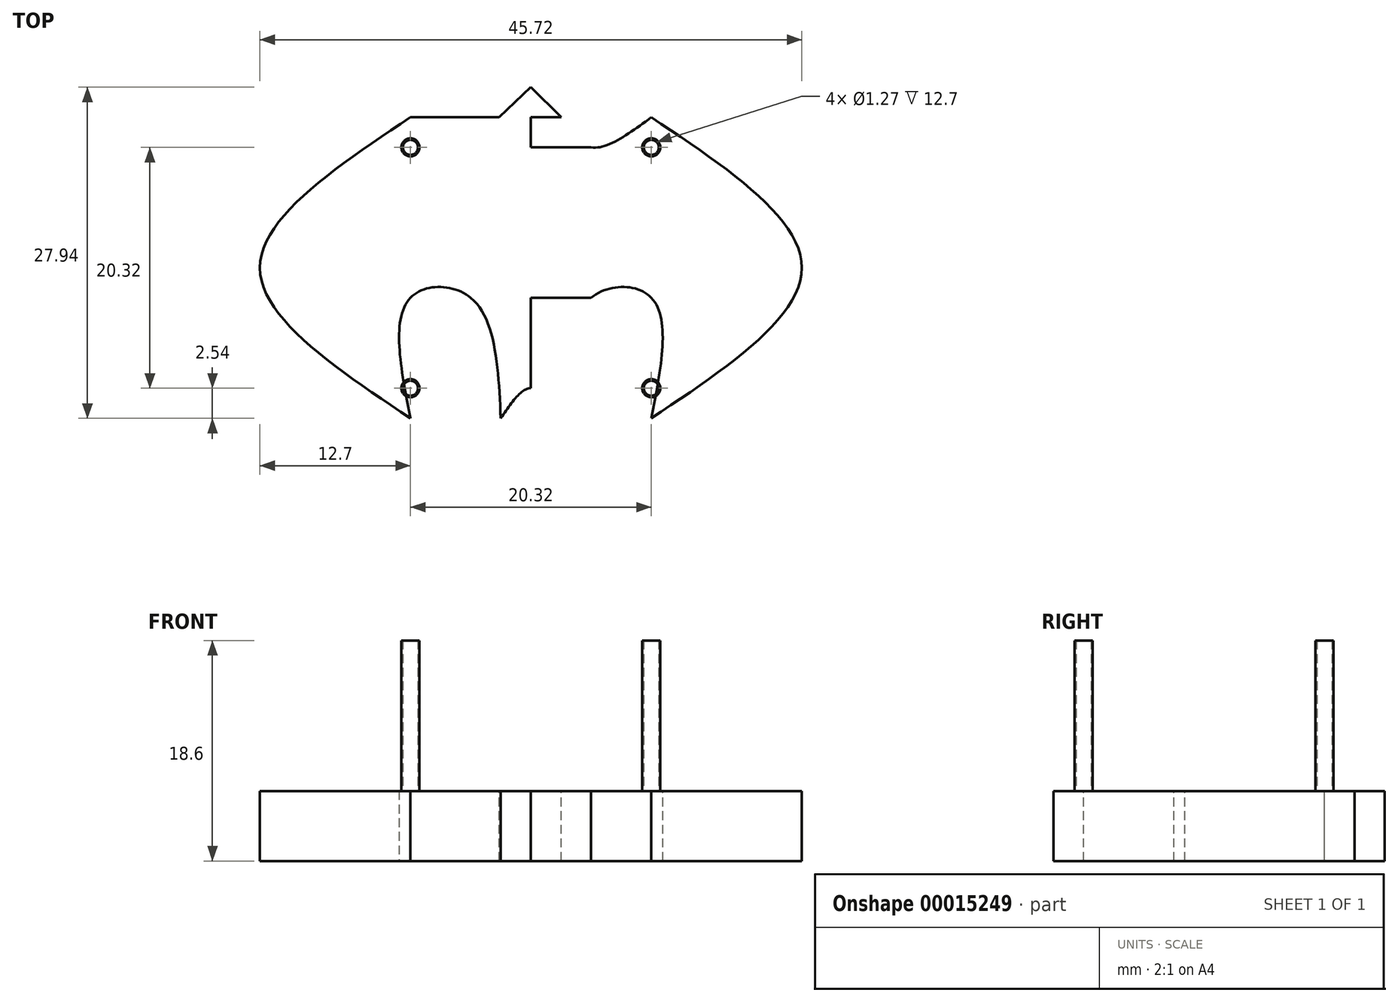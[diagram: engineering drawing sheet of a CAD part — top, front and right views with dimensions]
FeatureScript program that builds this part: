
annotation { "Feature Type Name" : "Feature", "Feature Type Description" : "" }
export const myFeature = defineFeature(function(context is Context, id is Id, definition is map)
    precondition{}
    {
        {
            var Q0;
            Q0=qCreatedBy(makeId("Top.planeOp"),FACE);
            var sketch = newSketch(context, id + "F0", { "sketchPlane" : qUnion([Q0])});
            skLineSegment(sketch, "E0.rect.bottom", {"start": v(10.16, 10.16) * mm, "end": v(-10.16, 10.16) * mm});
            skLineSegment(sketch, "E0.rect.top", {"start": v(10.16, -10.16) * mm, "end": v(-10.16, -10.16) * mm});
            skLineSegment(sketch, "E0.rect.left", {"start": v(10.16, 10.16) * mm, "end": v(10.16, -10.16) * mm});
            skLineSegment(sketch, "E0.rect.right", {"start": v(-10.16, 10.16) * mm, "end": v(-10.16, -10.16) * mm});
            skPoint(sketch, "E0.rect.middle", {"position": v(0, 0) * mm});
            skCircle(sketch, "E1", {"center": v(-10.16, 10.16) * mm, "radius": 0.64 * mm});
            skCircle(sketch, "E2", {"center": v(10.16, 10.16) * mm, "radius": 0.64 * mm});
            skCircle(sketch, "E3", {"center": v(-10.16, -10.16) * mm, "radius": 0.64 * mm});
            skCircle(sketch, "E4", {"center": v(10.16, -10.16) * mm, "radius": 0.64 * mm});
            skLineSegment(sketch, "E5", {"start": v(0, 0) * mm, "end": v(0, -12.7) * mm});
            skLineSegment(sketch, "E6", {"start": v(0, 0) * mm, "end": v(0, 12.7) * mm});
            skCircle(sketch, "E7", {"center": v(-10.16, 10.16) * mm, "radius": 0.76 * mm});
            skCircle(sketch, "E8", {"center": v(10.16, 10.16) * mm, "radius": 0.76 * mm});
            skCircle(sketch, "E9", {"center": v(-10.16, -10.16) * mm, "radius": 0.76 * mm});
            skCircle(sketch, "E10", {"center": v(10.16, -10.16) * mm, "radius": 0.76 * mm});
            skSolve(sketch);
        }
        {
            var Q0;
            {var subQ0=sQuery(id+"F0.wireOp",EDGE,"E9");var subQ3=sQuery(id+"F0.wireOp",EDGE,"E0.rect.top");var subQ4=makeQuery(id+"F0.imprint","INTERSECT",VERTEX,{"derivedFrom":[subQ3,subQ0]});Q0=makeQuery(id+"F0.imprint","IMPRINT",FACE,{"disambiguationData":[TD([[makeQuery(id+"F0.imprint","IMPRINT",EDGE,{"disambiguationData":[TD([[subQ4,-1.0]])],"derivedFrom":subQ3}),1.0]])]});}
            var Q1;
            {var subQ0=sQuery(id+"F0.wireOp",EDGE,"E10");var subQ3=sQuery(id+"F0.wireOp",EDGE,"E0.rect.top");var subQ4=makeQuery(id+"F0.imprint","INTERSECT",VERTEX,{"derivedFrom":[subQ3,subQ0]});Q1=makeQuery(id+"F0.imprint","IMPRINT",FACE,{"disambiguationData":[TD([[makeQuery(id+"F0.imprint","IMPRINT",EDGE,{"disambiguationData":[TD([[subQ4,1.0]])],"derivedFrom":subQ3}),-1.0]])]});}
            var Q2;
            {var subQ0=sQuery(id+"F0.wireOp",EDGE,"E9");var subQ3=sQuery(id+"F0.wireOp",EDGE,"E0.rect.top");var subQ4=makeQuery(id+"F0.imprint","INTERSECT",VERTEX,{"derivedFrom":[subQ3,subQ0]});Q2=makeQuery(id+"F0.imprint","IMPRINT",FACE,{"disambiguationData":[TD([[makeQuery(id+"F0.imprint","IMPRINT",EDGE,{"disambiguationData":[TD([[subQ4,-1.0]])],"derivedFrom":subQ3}),-1.0]])]});}
            var Q3;
            {var subQ0=sQuery(id+"F0.wireOp",EDGE,"E10");var subQ3=sQuery(id+"F0.wireOp",EDGE,"E0.rect.top");var subQ4=makeQuery(id+"F0.imprint","INTERSECT",VERTEX,{"derivedFrom":[subQ3,subQ0]});Q3=makeQuery(id+"F0.imprint","IMPRINT",FACE,{"disambiguationData":[TD([[makeQuery(id+"F0.imprint","IMPRINT",EDGE,{"disambiguationData":[TD([[subQ4,1.0]])],"derivedFrom":subQ3}),1.0]])]});}
            var Q4;
            {var subQ0=sQuery(id+"F0.wireOp",EDGE,"E7");var subQ3=sQuery(id+"F0.wireOp",EDGE,"E0.rect.bottom");var subQ4=makeQuery(id+"F0.imprint","INTERSECT",VERTEX,{"derivedFrom":[subQ3,subQ0]});Q4=makeQuery(id+"F0.imprint","IMPRINT",FACE,{"disambiguationData":[TD([[makeQuery(id+"F0.imprint","IMPRINT",EDGE,{"disambiguationData":[TD([[subQ4,-1.0]])],"derivedFrom":subQ3}),1.0]])]});}
            var Q5;
            {var subQ0=sQuery(id+"F0.wireOp",EDGE,"E7");var subQ3=sQuery(id+"F0.wireOp",EDGE,"E0.rect.bottom");var subQ4=makeQuery(id+"F0.imprint","INTERSECT",VERTEX,{"derivedFrom":[subQ3,subQ0]});Q5=makeQuery(id+"F0.imprint","IMPRINT",FACE,{"disambiguationData":[TD([[makeQuery(id+"F0.imprint","IMPRINT",EDGE,{"disambiguationData":[TD([[subQ4,-1.0]])],"derivedFrom":subQ3}),-1.0]])]});}
            var Q6;
            {var subQ0=sQuery(id+"F0.wireOp",EDGE,"E8");var subQ3=sQuery(id+"F0.wireOp",EDGE,"E0.rect.bottom");var subQ4=makeQuery(id+"F0.imprint","INTERSECT",VERTEX,{"derivedFrom":[subQ3,subQ0]});Q6=makeQuery(id+"F0.imprint","IMPRINT",FACE,{"disambiguationData":[TD([[makeQuery(id+"F0.imprint","IMPRINT",EDGE,{"disambiguationData":[TD([[subQ4,1.0]])],"derivedFrom":subQ3}),-1.0]])]});}
            var Q7;
            {var subQ0=sQuery(id+"F0.wireOp",EDGE,"E8");var subQ3=sQuery(id+"F0.wireOp",EDGE,"E0.rect.bottom");var subQ4=makeQuery(id+"F0.imprint","INTERSECT",VERTEX,{"derivedFrom":[subQ3,subQ0]});Q7=makeQuery(id+"F0.imprint","IMPRINT",FACE,{"disambiguationData":[TD([[makeQuery(id+"F0.imprint","IMPRINT",EDGE,{"disambiguationData":[TD([[subQ4,1.0]])],"derivedFrom":subQ3}),1.0]])]});}
            extrude(context, id + "F1", {"entities" : qUnion([Q0, Q1, Q2, Q3, Q4, Q5, Q6, Q7]), "depth" : 12.7 * mm});
        }
        {
            var Q0;
            Q0=qCreatedBy(makeId("Top.planeOp"),FACE);
            var sketch = newSketch(context, id + "F2", { "sketchPlane" : qUnion([Q0])});
            skLineSegment(sketch, "E11", {"start": v(0, 0) * mm, "end": v(-22.86, 0) * mm});
            skLineSegment(sketch, "E12", {"start": v(0, 0) * mm, "end": v(22.86, 0) * mm});
            skLineSegment(sketch, "E13", {"start": v(0, 0) * mm, "end": v(0, 12.7) * mm});
            skLineSegment(sketch, "E14", {"start": v(0, 0) * mm, "end": v(0, -12.7) * mm});
            skLineSegment(sketch, "E15", {"start": v(0, 12.7) * mm, "end": v(-10.16, 12.7) * mm});
            skLineSegment(sketch, "E16", {"start": v(0, 12.7) * mm, "end": v(10.16, 12.7) * mm});
            skLineSegment(sketch, "E17", {"start": v(0, -12.7) * mm, "end": v(-10.16, -12.7) * mm});
            skLineSegment(sketch, "E18", {"start": v(0, -12.7) * mm, "end": v(10.16, -12.7) * mm});
            skFitSpline(sketch, "E19", {"points": [v(-10.16, 12.7) * mm, v(-22.86, 0) * mm, v(-10.16, -12.7) * mm], "startDerivative": vector(-38.1, -25.4) * mm, "endDerivative": vector(38.1, -25.4) * mm});
            skFitSpline(sketch, "E20", {"points": [v(10.16, -12.7) * mm, v(22.86, 0) * mm, v(10.16, 12.7) * mm], "startDerivative": vector(38.1, 25.4) * mm, "endDerivative": vector(-38.1, 25.4) * mm});
            skLineSegment(sketch, "E21", {"start": v(0, -2.53) * mm, "end": v(-10.16, -2.53) * mm});
            skLineSegment(sketch, "E22", {"start": v(0, 2.54) * mm, "end": v(-10.16, 2.54) * mm});
            skLineSegment(sketch, "E23", {"start": v(0, -2.53) * mm, "end": v(10.16, -2.53) * mm});
            skLineSegment(sketch, "E24", {"start": v(0, -12.7) * mm, "end": v(-2.54, -12.7) * mm});
            skLineSegment(sketch, "E25", {"start": v(0, -12.7) * mm, "end": v(2.54, -12.7) * mm});
            skLineSegment(sketch, "E26", {"start": v(0, -12.7) * mm, "end": v(0, -10.16) * mm});
            skFitSpline(sketch, "E27", {"points": [v(-2.54, -12.7) * mm, v(0, -10.16) * mm, v(2.54, -12.7) * mm], "startDerivative": vector(5.08, 7.62) * mm, "endDerivative": vector(5.08, -7.62) * mm});
            skLineSegment(sketch, "E28", {"start": v(0, -2.53) * mm, "end": v(5.08, -2.53) * mm});
            skFitSpline(sketch, "E29", {"points": [v(10.16, -12.7) * mm, v(10.16, -2.53) * mm, v(5.08, -2.53) * mm, v(2.54, -12.7) * mm], "startDerivative": vector(6.79, 34.44) * mm, "endDerivative": vector(-1.64, -33.9) * mm});
            skLineSegment(sketch, "E30", {"start": v(0, 12.7) * mm, "end": v(0, 10.16) * mm});
            skLineSegment(sketch, "E31", {"start": v(0, 10.16) * mm, "end": v(-5.08, 10.16) * mm});
            skLineSegment(sketch, "E32", {"start": v(0, 10.16) * mm, "end": v(5.08, 10.16) * mm});
            skLineSegment(sketch, "E33", {"start": v(0, 12.7) * mm, "end": v(0, 15.24) * mm});
            skLineSegment(sketch, "E34", {"start": v(0, 12.7) * mm, "end": v(-2.68, 12.7) * mm});
            skLineSegment(sketch, "E35", {"start": v(0, 12.7) * mm, "end": v(2.56, 12.7) * mm});
            skFitSpline(sketch, "E36", {"points": [v(-10.16, 12.7) * mm, v(-5.08, 10.16) * mm, v(-2.68, 12.7) * mm, v(-2.68, 12.7) * mm], "startDerivative": vector(10.07, -7.42) * mm, "endDerivative": vector(4.67, 8.04) * mm});
            skFitSpline(sketch, "E37", {"points": [v(10.16, 12.7) * mm, v(5.08, 10.16) * mm, v(2.56, 12.7) * mm], "startDerivative": vector(-10.06, -7.43) * mm, "endDerivative": vector(-4.95, 8.02) * mm});
            skLineSegment(sketch, "E38", {"start": v(-2.68, 12.7) * mm, "end": v(0, 15.24) * mm});
            skLineSegment(sketch, "E39", {"start": v(2.56, 12.7) * mm, "end": v(0, 15.24) * mm});
            skFitSpline(sketch, "E40", {"points": [v(-10.16, -12.7) * mm, v(-10.16, -2.53) * mm, v(-5.08, -2.53) * mm, v(-2.54, -12.7) * mm], "startDerivative": vector(-6.79, 34.44) * mm, "endDerivative": vector(1.64, -33.9) * mm});
            skSolve(sketch);
        }
        {
            var Q0;
            {var subQ5=sQuery(id+"F2.wireOp",EDGE,"E12");Q0=makeQuery(id+"F2.imprint","IMPRINT",FACE,{"disambiguationData":[TD([[makeQuery(id+"F2.imprint","IMPRINT",EDGE,{"derivedFrom":subQ5}),-1.0]])]});}
            var Q1;
            {var subQ8=sQuery(id+"F2.wireOp",EDGE,"E11");Q1=makeQuery(id+"F2.imprint","IMPRINT",FACE,{"disambiguationData":[TD([[makeQuery(id+"F2.imprint","IMPRINT",EDGE,{"derivedFrom":subQ8}),1.0]])]});}
            var Q2;
            {var subQ4=sQuery(id+"F2.wireOp",EDGE,"E11");Q2=makeQuery(id+"F2.imprint","IMPRINT",FACE,{"disambiguationData":[TD([[makeQuery(id+"F2.imprint","IMPRINT",EDGE,{"derivedFrom":subQ4}),-1.0]])]});}
            var Q3;
            Q3=makeQuery(id+"F2.imprint","IMPRINT",FACE,{"disambiguationData":[TD([[makeQuery(id+"F2.imprint","IMPRINT",EDGE,{"derivedFrom":sQuery(id+"F2.wireOp",EDGE,"E30")}),1.0]])]});
            var Q4;
            {var subQ0=sQuery(id+"F2.wireOp",EDGE,"E40");var subQ1=sQuery(id+"F2.wireOp",EDGE,"E21");var subQ2=makeQuery(id+"F2.imprint","INTERSECT",VERTEX,{"disambiguationData":[OD(1.0)],"derivedFrom":[subQ1,subQ0]});Q4=makeQuery(id+"F2.imprint","IMPRINT",FACE,{"disambiguationData":[TD([[makeQuery(id+"F2.imprint","IMPRINT",EDGE,{"disambiguationData":[TD([[subQ2,1.0]])],"derivedFrom":subQ1}),1.0]])]});}
            var Q5;
            Q5=makeQuery(id+"F2.imprint","IMPRINT",FACE,{"disambiguationData":[TD([[makeQuery(id+"F2.imprint","IMPRINT",EDGE,{"derivedFrom":sQuery(id+"F2.wireOp",EDGE,"E33")}),1.0]])]});
            var Q6;
            {var subQ4=sQuery(id+"F2.wireOp",EDGE,"E12");Q6=makeQuery(id+"F2.imprint","IMPRINT",FACE,{"disambiguationData":[TD([[makeQuery(id+"F2.imprint","IMPRINT",EDGE,{"derivedFrom":subQ4}),1.0]])]});}
            var Q7;
            Q7=makeQuery(id+"F2.imprint","IMPRINT",FACE,{"disambiguationData":[TD([[makeQuery(id+"F2.imprint","IMPRINT",EDGE,{"derivedFrom":sQuery(id+"F2.wireOp",EDGE,"E33")}),-1.0]])]});
            var Q8;
            {var subQ1=sQuery(id+"F2.wireOp",EDGE,"E28");Q8=makeQuery(id+"F2.imprint","IMPRINT",FACE,{"disambiguationData":[TD([[makeQuery(id+"F2.imprint","IMPRINT",EDGE,{"derivedFrom":subQ1}),-1.0]])]});}
            var Q9;
            Q9=makeQuery(id+"F2.imprint","IMPRINT",FACE,{"disambiguationData":[TD([[makeQuery(id+"F2.imprint","IMPRINT",EDGE,{"derivedFrom":sQuery(id+"F2.wireOp",EDGE,"E30")}),-1.0]])]});
            extrude(context, id + "F3", {"entities" : qUnion([Q0, Q1, Q2, Q3, Q4, Q5, Q6, Q7, Q8, Q9]), "oppositeDirection" : true, "depth" : 5.9 * mm});
        }
    });
